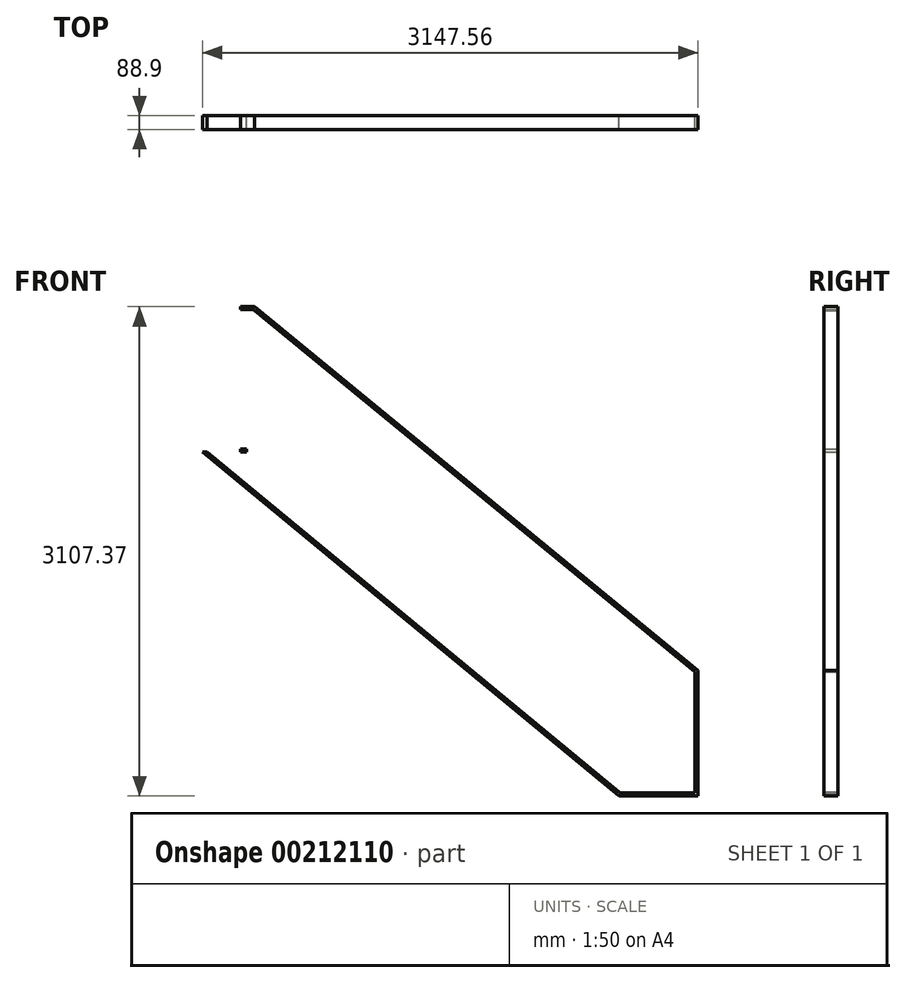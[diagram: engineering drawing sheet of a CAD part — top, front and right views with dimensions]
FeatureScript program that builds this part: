
annotation { "Feature Type Name" : "Feature", "Feature Type Description" : "" }
export const myFeature = defineFeature(function(context is Context, id is Id, definition is map)
    precondition{}
    {
        {
            var Q0;
            Q0=qCreatedBy(makeId("Front.planeOp"),FACE);
            var sketch = newSketch(context, id + "F0", { "sketchPlane" : qUnion([Q0])});
            skLineSegment(sketch, "E0", {"start": v(0, 0) * mm, "end": v(-381, 0) * mm});
            skLineSegment(sketch, "E1", {"start": v(-381, 0) * mm, "end": v(-3172.96, 2305.05) * mm});
            skLineSegment(sketch, "E2", {"start": v(-3172.96, 2305.05) * mm, "end": v(-2931.66, 2305.05) * mm});
            skLineSegment(sketch, "E3", {"start": v(-2931.66, 2305.05) * mm, "end": v(-2931.66, 3333.75) * mm});
            skLineSegment(sketch, "E4", {"start": v(-2931.66, 3333.75) * mm, "end": v(0, 930.27) * mm});
            skLineSegment(sketch, "E5", {"start": v(0, 930.27) * mm, "end": v(0, 0) * mm});
            skLineSegment(sketch, "E6", {"start": v(0, 107.95) * mm, "end": v(-511.75, 107.95) * mm});
            skSolve(sketch);
        }
        {
            var Q0;
            {var subQ1=sQuery(id+"F0.wireOp",EDGE,"E2");Q0=makeQuery(id+"F0.imprint","IMPRINT",FACE,{"disambiguationData":[TD([[makeQuery(id+"F0.imprint","IMPRINT",EDGE,{"derivedFrom":subQ1}),-1.0]])]});}
            var sketch = newSketch(context, id + "F1", { "sketchPlane" : qUnion([Q0])});
            skLineSegment(sketch, "E7.0", {"start": v(-2931.66, 3333.75) * mm, "end": v(0, 930.27) * mm});
            skLineSegment(sketch, "E8.0", {"start": v(-2931.66, 2305.05) * mm, "end": v(-2931.66, 3333.75) * mm});
            skLineSegment(sketch, "E9", {"start": v(-2842.76, 3228.02) * mm, "end": v(-2842.76, 3203.39) * mm});
            skLineSegment(sketch, "E10", {"start": v(-2842.76, 3203.39) * mm, "end": v(-44.45, 909.24) * mm});
            skLineSegment(sketch, "E11", {"start": v(-44.45, 909.24) * mm, "end": v(-44.45, 933.87) * mm});
            skLineSegment(sketch, "E12", {"start": v(-44.45, 933.87) * mm, "end": v(-2842.76, 3228.02) * mm});
            skLineSegment(sketch, "E13.bottom", {"start": v(-2842.76, 3228.02) * mm, "end": v(-2931.66, 3228.02) * mm});
            skLineSegment(sketch, "E13.top", {"start": v(-2842.76, 3208.97) * mm, "end": v(-2931.66, 3208.97) * mm});
            skLineSegment(sketch, "E13.left", {"start": v(-2842.76, 3228.02) * mm, "end": v(-2842.76, 3208.97) * mm});
            skLineSegment(sketch, "E13.right", {"start": v(-2931.66, 3228.02) * mm, "end": v(-2931.66, 3208.97) * mm});
            skLineSegment(sketch, "E14.bottom", {"start": v(-44.45, 933.87) * mm, "end": v(-25.4, 933.87) * mm});
            skLineSegment(sketch, "E14.top", {"start": v(-44.45, 120.65) * mm, "end": v(-25.4, 120.65) * mm});
            skLineSegment(sketch, "E14.left", {"start": v(-44.45, 933.87) * mm, "end": v(-44.45, 120.65) * mm});
            skLineSegment(sketch, "E14.right", {"start": v(-25.4, 933.87) * mm, "end": v(-25.4, 120.65) * mm});
            skLineSegment(sketch, "E15", {"start": v(-44.45, 933.87) * mm, "end": v(-25.4, 918.25) * mm});
            skLineSegment(sketch, "E16.bottom", {"start": v(-44.45, 120.65) * mm, "end": v(-527.14, 120.65) * mm});
            skLineSegment(sketch, "E16.top", {"start": v(-44.45, 139.7) * mm, "end": v(-527.14, 139.7) * mm});
            skLineSegment(sketch, "E16.left", {"start": v(-44.45, 120.65) * mm, "end": v(-44.45, 139.7) * mm});
            skLineSegment(sketch, "E16.right", {"start": v(-527.14, 120.65) * mm, "end": v(-527.14, 139.7) * mm});
            skLineSegment(sketch, "E17", {"start": v(-527.14, 120.65) * mm, "end": v(-3172.96, 2305.05) * mm});
            skLineSegment(sketch, "E18", {"start": v(-3143.03, 2305.05) * mm, "end": v(-527.14, 145.35) * mm});
            skLineSegment(sketch, "E19", {"start": v(-527.14, 145.35) * mm, "end": v(-527.14, 139.7) * mm});
            skLineSegment(sketch, "E20", {"start": v(-2931.66, 2305.05) * mm, "end": v(-2912.6, 2305.05) * mm});
            skLineSegment(sketch, "E21.bottom", {"start": v(-2931.66, 2305.05) * mm, "end": v(-2893.56, 2305.05) * mm});
            skLineSegment(sketch, "E21.top", {"start": v(-2931.66, 2324.1) * mm, "end": v(-2893.56, 2324.1) * mm});
            skLineSegment(sketch, "E21.left", {"start": v(-2931.66, 2305.05) * mm, "end": v(-2931.66, 2324.1) * mm});
            skLineSegment(sketch, "E21.right", {"start": v(-2893.56, 2305.05) * mm, "end": v(-2893.56, 2324.1) * mm});
            skLineSegment(sketch, "E22", {"start": v(-3172.96, 2305.05) * mm, "end": v(-3143.03, 2305.05) * mm});
            skSolve(sketch);
        }
        {
            var Q0;
            Q0=makeQuery(id+"F1.imprint","IMPRINT",FACE,{"disambiguationData":[TD([[makeQuery(id+"F1.imprint","IMPRINT",EDGE,{"derivedFrom":sQuery(id+"F1.wireOp",EDGE,"E13.bottom")}),1.0]])]});
            extrude(context, id + "F2", {"entities" : qUnion([Q0]), "depth" : 88.9 * mm});
        }
        {
            var Q0;
            Q0=makeQuery(id+"F1.imprint","IMPRINT",FACE,{"disambiguationData":[TD([[makeQuery(id+"F1.imprint","IMPRINT",EDGE,{"derivedFrom":sQuery(id+"F1.wireOp",EDGE,"E9")}),1.0]])]});
            extrude(context, id + "F3", {"entities" : qUnion([Q0]), "operationType" : NewBodyOperationType.ADD, "depth" : 88.9 * mm});
        }
        {
            var Q0;
            {var subQ1=sQuery(id+"F1.wireOp",EDGE,"E14.top");Q0=makeQuery(id+"F1.imprint","IMPRINT",FACE,{"disambiguationData":[TD([[makeQuery(id+"F1.imprint","IMPRINT",EDGE,{"derivedFrom":subQ1}),1.0]])]});}
            extrude(context, id + "F4", {"entities" : qUnion([Q0]), "operationType" : NewBodyOperationType.ADD, "depth" : 88.9 * mm});
        }
        {
            var Q0;
            Q0=makeQuery(id+"F1.imprint","IMPRINT",FACE,{"disambiguationData":[TD([[makeQuery(id+"F1.imprint","IMPRINT",EDGE,{"derivedFrom":sQuery(id+"F1.wireOp",EDGE,"E16.bottom")}),-1.0]])]});
            extrude(context, id + "F5", {"entities" : qUnion([Q0]), "operationType" : NewBodyOperationType.ADD, "depth" : 88.9 * mm});
        }
        {
            var Q0;
            Q0=makeQuery(id+"F1.imprint","IMPRINT",FACE,{"disambiguationData":[TD([[makeQuery(id+"F1.imprint","IMPRINT",EDGE,{"derivedFrom":sQuery(id+"F1.wireOp",EDGE,"E16.right")}),1.0]])]});
            extrude(context, id + "F6", {"entities" : qUnion([Q0]), "operationType" : NewBodyOperationType.ADD, "depth" : 88.9 * mm});
        }
        {
            var Q0;
            Q0=makeQuery(id+"F1.imprint","IMPRINT",FACE,{"disambiguationData":[TD([[makeQuery(id+"F1.imprint","IMPRINT",EDGE,{"derivedFrom":sQuery(id+"F1.wireOp",EDGE,"E21.top")}),-1.0]])]});
            extrude(context, id + "F7", {"entities" : qUnion([Q0]), "depth" : 88.9 * mm});
        }
    });
